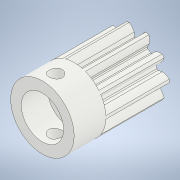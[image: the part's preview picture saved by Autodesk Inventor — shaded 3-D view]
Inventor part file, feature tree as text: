
AUTODESK INVENTOR PART (.ipt)
format: ipt  version: 2022 (Build 260153000, 153)  size: 644,096 bytes
history: native  units: in
note: dims shown in document units (in); Inventor stores cm internally (conversion verified against a paired STEP export)
features: extrude x5, sketch x4, projected_geometry x3
ambient origin geometry x8: Origin, YZ Plane, XZ Plane, XY Plane, X Axis, Y Axis, Z Axis, Center Point
bodies: Solid1 (feature_tree), Body1 (feature_tree)
feature tree (12):
  extrude  "Extrusion1"  Depth=0.3937in TaperAngle=0.0deg
  sketch  "Sketch3"  dims[d6=0.315in d8=0.0787in]
  extrude  "Extrusion2"  Depth=0.0787in
  extrude  "Extrusion3"  Depth=0.2362in TaperAngle=0.0deg
  extrude  "Extrusion4"  Depth=0.0787in TaperAngle=0.0deg
  extrude  "Extrusion5"  Depth=0.0787in TaperAngle=0.0deg
  sketch  "Sketch1"  dims[d0=0.2165in d1=0.3937in d2=0.0in]
  projected_geometry  "Projected Loop1"
  sketch  "Sketch4"  dims[d9=0.0394in d10=0.0in d11=0.2362in d12=0.0in]
  projected_geometry  "Projected Loop2"
  sketch  "Sketch5"  dims[d13=0.0984in d14=0.6112in d15=0.0in d16=0.0787in d17=0.0in]
  projected_geometry  "Projected Loop3"
